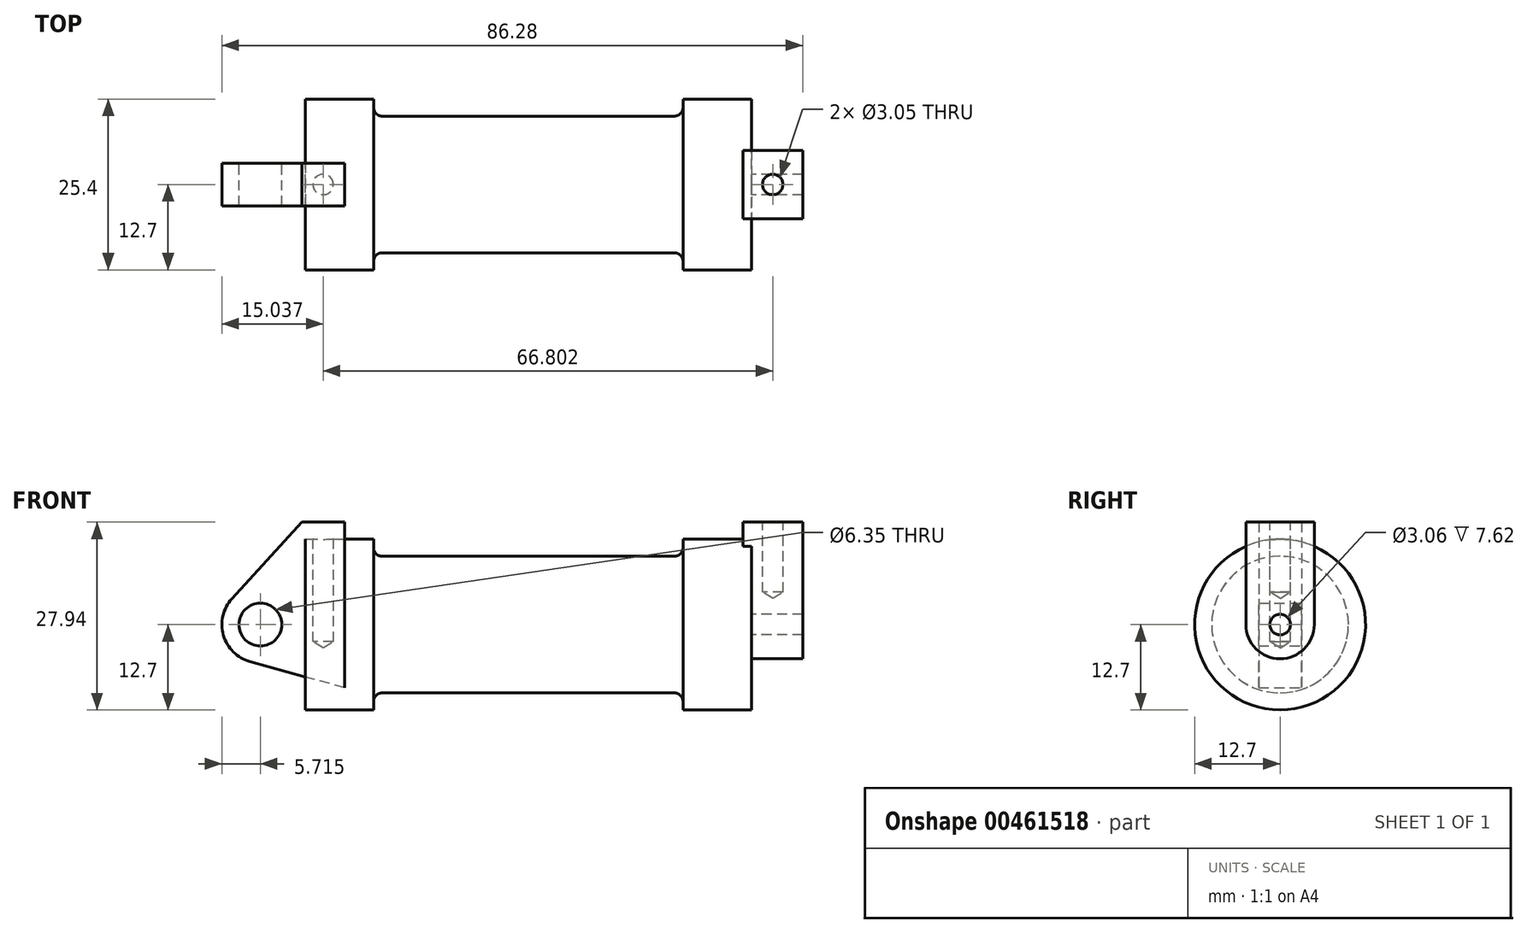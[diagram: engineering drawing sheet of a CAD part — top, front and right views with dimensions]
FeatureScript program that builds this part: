
annotation { "Feature Type Name" : "Feature", "Feature Type Description" : "" }
export const myFeature = defineFeature(function(context is Context, id is Id, definition is map)
    precondition{}
    {
        {
            var Q0;
            Q0=qCreatedBy(makeId("Front.planeOp"),FACE);
            var sketch = newSketch(context, id + "F0", { "sketchPlane" : qUnion([Q0])});
            skLineSegment(sketch, "E0", {"start": v(0, 0) * mm, "end": v(0, 12.7) * mm});
            skLineSegment(sketch, "E1", {"start": v(0, 12.7) * mm, "end": v(10.16, 12.7) * mm});
            skLineSegment(sketch, "E2", {"start": v(10.16, 12.7) * mm, "end": v(10.16, 10.16) * mm});
            skLineSegment(sketch, "E3", {"start": v(10.16, 10.16) * mm, "end": v(56.13, 10.16) * mm});
            skLineSegment(sketch, "E4", {"start": v(56.13, 10.16) * mm, "end": v(56.13, 12.7) * mm});
            skLineSegment(sketch, "E5", {"start": v(56.13, 12.7) * mm, "end": v(66.3, 12.7) * mm});
            skLineSegment(sketch, "E6", {"start": v(66.3, 12.7) * mm, "end": v(66.3, 0) * mm});
            skLineSegment(sketch, "E7", {"start": v(66.3, 0) * mm, "end": v(0, 0) * mm});
            skLineSegment(sketch, "E8", {"start": v(5.84, 15.24) * mm, "end": v(-0.5, 15.24) * mm});
            skLineSegment(sketch, "E9", {"start": v(-0.5, 15.24) * mm, "end": v(-10.88, 3.85) * mm});
            skLineSegment(sketch, "E10", {"start": v(0, 0) * mm, "end": v(-6.65, 0) * mm});
            skCircle(sketch, "E11", {"center": v(-6.65, 0) * mm, "radius": 5.72 * mm});
            skCircle(sketch, "E12", {"center": v(-6.65, 0) * mm, "radius": 3.18 * mm});
            skLineSegment(sketch, "E13", {"start": v(5.84, 15.24) * mm, "end": v(5.84, -9.4) * mm});
            skLineSegment(sketch, "E14", {"start": v(5.84, -9.4) * mm, "end": v(-8.18, -5.5) * mm});
            skSolve(sketch);
        }
        {
            var Q0;
            {var subQ0=sQuery(id+"F0.wireOp",EDGE,"E2");Q0=makeQuery(id+"F0.imprint","IMPRINT",FACE,{"disambiguationData":[TD([[makeQuery(id+"F0.imprint","IMPRINT",EDGE,{"derivedFrom":subQ0}),-1.0]])]});}
            var Q1;
            {var subQ0=sQuery(id+"F0.wireOp",EDGE,"E0");Q1=makeQuery(id+"F0.imprint","IMPRINT",FACE,{"disambiguationData":[TD([[makeQuery(id+"F0.imprint","IMPRINT",EDGE,{"derivedFrom":subQ0}),-1.0]])]});}
            var Q2;
            Q2=sQuery(id+"F0.wireOp",EDGE,"E7");
            revolve(context, id + "F1", {"entities" : qUnion([Q0, Q1]), "axis" : qUnion([Q2]), "revolveType" : RevolveType.FULL});
        }
        {
            var Q0;
            {var subQ4=sQuery(id+"F0.wireOp",EDGE,"E12");Q0=makeQuery(id+"F0.imprint","IMPRINT",FACE,{"disambiguationData":[TD([[makeQuery(id+"F0.imprint","IMPRINT",EDGE,{"derivedFrom":subQ4}),-1.0]])]});}
            var Q1;
            {var subQ0=sQuery(id+"F0.wireOp",EDGE,"E14");Q1=makeQuery(id+"F0.imprint","IMPRINT",FACE,{"disambiguationData":[TD([[makeQuery(id+"F0.imprint","IMPRINT",EDGE,{"derivedFrom":subQ0}),-1.0]])]});}
            var Q2;
            {var subQ3=sQuery(id+"F0.wireOp",EDGE,"E0");Q2=makeQuery(id+"F0.imprint","IMPRINT",FACE,{"disambiguationData":[TD([[makeQuery(id+"F0.imprint","IMPRINT",EDGE,{"derivedFrom":subQ3}),1.0]])]});}
            var Q3;
            {var subQ0=sQuery(id+"F0.wireOp",EDGE,"E0");Q3=makeQuery(id+"F0.imprint","IMPRINT",FACE,{"disambiguationData":[TD([[makeQuery(id+"F0.imprint","IMPRINT",EDGE,{"derivedFrom":subQ0}),-1.0]])]});}
            extrude(context, id + "F2", {"entities" : qUnion([Q0, Q1, Q2, Q3]), "endBound" : BoundingType.SYMMETRIC, "depth" : (25.4 * 0.25) * mm});
        }
        {
            var Q0;
            Q0=makeQuery(id+"F1.opRevolve","SWEPT_FACE",FACE,{"disambiguationData":[OSD([sQuery(id+"F0.wireOp",EDGE,"E6")])]});
            var sketch = newSketch(context, id + "F3", { "sketchPlane" : qUnion([Q0])});
            skCircle(sketch, "E15", {"center": v(0, 0) * mm, "radius": 1.53 * mm});
            skCircle(sketch, "E16", {"center": v(0, 0) * mm, "radius": 5.08 * mm});
            skLineSegment(sketch, "E17", {"start": v(-5.08, 0) * mm, "end": v(-5.08, 15.24) * mm});
            skLineSegment(sketch, "E18", {"start": v(-5.08, 15.24) * mm, "end": v(-5.08, 15.24) * mm});
            skLineSegment(sketch, "E19", {"start": v(5.08, 0) * mm, "end": v(5.08, 15.24) * mm});
            skLineSegment(sketch, "E20", {"start": v(5.08, 15.24) * mm, "end": v(-5.08, 15.24) * mm});
            skSolve(sketch);
        }
        {
            var Q0;
            Q0=qSketchRegion(id+"F3",true);
            extrude(context, id + "F4", {"entities" : qUnion([Q0]), "operationType" : NewBodyOperationType.ADD, "depth" : (25.4 * 0.3) * mm, "hasSecondDirection" : true, "secondDirectionOppositeDirection" : true, "secondDirectionDepth" : (25.4 * 0.05) * mm});
        }
        {
            var Q0;
            Q0=makeQuery(id+"F2.opExtrude","SWEPT_FACE",FACE,{"disambiguationData":[OSD([sQuery(id+"F0.wireOp",EDGE,"E8")])]});
            var sketch = newSketch(context, id + "F5", { "sketchPlane" : qUnion([Q0])});
            skPoint(sketch, "E21", {"position": v(2.67, 0) * mm});
            skLineSegment(sketch, "E22", {"start": v(2.67, 3.17) * mm, "end": v(2.67, -3.17) * mm, "construction": true});
            skLineSegment(sketch, "E23", {"start": v(-0.5, 0) * mm, "end": v(5.84, 0) * mm, "construction": true});
            skSolve(sketch);
        }
        {
            var Q0;
            Q0=sQuery(id+"F5.wireOp",VERTEX,"E21");
            var Q1;
            Q1=makeQuery(id+"F1.opRevolve","SWEPT_BODY",BODY,{"disambiguationData":[OSD([sQuery(id+"F0.wireOp",EDGE,"E0"),sQuery(id+"F0.wireOp",EDGE,"E1"),sQuery(id+"F0.wireOp",EDGE,"E2"),sQuery(id+"F0.wireOp",EDGE,"E3"),sQuery(id+"F0.wireOp",EDGE,"E4"),sQuery(id+"F0.wireOp",EDGE,"E5"),sQuery(id+"F0.wireOp",EDGE,"E6"),sQuery(id+"F0.wireOp",EDGE,"E7")])]});
            hole(context, id + "F6", {"style" : HoleStyle.SIMPLE, "endStyle" : HoleEndStyle.BLIND, "holeDiameter" : (25.4 * 0.12) * mm, "holeDepth" : (25.4 * 0.7) * mm, "startFromSketch" : true, "locations" : qUnion([Q0]), "scope" : qUnion([Q1])});
        }
        {
            var Q0;
            Q0=makeQuery(id+"F4.opExtrude","SWEPT_FACE",FACE,{"disambiguationData":[OSD([sQuery(id+"F3.wireOp",EDGE,"E20")])]});
            var sketch = newSketch(context, id + "F7", { "sketchPlane" : qUnion([Q0])});
            skLineSegment(sketch, "E24", {"start": v(69.47, 5.08) * mm, "end": v(69.47, -5.08) * mm, "construction": true});
            skLineSegment(sketch, "E25", {"start": v(73.91, 0) * mm, "end": v(65.02, 0) * mm, "construction": true});
            skPoint(sketch, "E26", {"position": v(69.47, 0) * mm});
            skSolve(sketch);
        }
        {
            var Q0;
            Q0=sQuery(id+"F7.wireOp",VERTEX,"E26");
            var Q1;
            Q1=makeQuery(id+"F1.opRevolve","SWEPT_BODY",BODY,{"disambiguationData":[OSD([sQuery(id+"F0.wireOp",EDGE,"E0"),sQuery(id+"F0.wireOp",EDGE,"E1"),sQuery(id+"F0.wireOp",EDGE,"E2"),sQuery(id+"F0.wireOp",EDGE,"E3"),sQuery(id+"F0.wireOp",EDGE,"E4"),sQuery(id+"F0.wireOp",EDGE,"E5"),sQuery(id+"F0.wireOp",EDGE,"E6"),sQuery(id+"F0.wireOp",EDGE,"E7")])]});
            hole(context, id + "F8", {"style" : HoleStyle.SIMPLE, "endStyle" : HoleEndStyle.BLIND, "holeDiameter" : (25.4 * 0.12) * mm, "holeDepth" : (25.4 * 0.4) * mm, "startFromSketch" : true, "locations" : qUnion([Q0]), "scope" : qUnion([Q1])});
        }
        {
            var Q0;
            Q0=makeQuery(id+"F1.opRevolve","SWEPT_FACE",FACE,{"disambiguationData":[OSD([sQuery(id+"F0.wireOp",EDGE,"E3")])]});
            fillet(context, id + "F9", {"entities" : qUnion([Q0]), "radius" : (25.4 * 0.05) * mm, "tangentPropagation" : true, "allowEdgeOverflow" : false});
        }
    });
